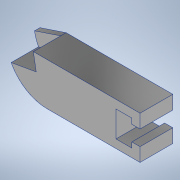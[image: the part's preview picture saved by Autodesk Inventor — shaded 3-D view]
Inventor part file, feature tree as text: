
AUTODESK INVENTOR PART (.ipt)
format: ipt  version: 2022 (Build 260153000, 153)  size: 172,032 bytes
history: native  units: mm
features: extrude x4, sketch x4, fillet x1
ambient origin geometry x8: Origin, YZ Plane, XZ Plane, XY Plane, X Axis, Y Axis, Z Axis, Center Point
bodies: Body1 (feature_tree)
feature tree (9):
  extrude  "Extrusion2"  Depth=5.8mm
  extrude  "Extrusion7"  Depth=12.0mm TaperAngle=0.0deg
  extrude  "Extrusion10"  Depth=15.6mm
  fillet  "Fillet2"  [1 undecoded]
  extrude  "Extrusion11"  Depth=5.6mm
  sketch  "Sketch5"  dims[d41=5.8mm d48=44.0mm]
  sketch  "Sketch11"  dims[d50=3.0mm d56=12.0mm d57=0.0mm]
  sketch  "Sketch14"  dims[d63=45.0mm d67=15.6mm d71=0.0mm]
  sketch  "Sketch15"  dims[d72=36.2mm d87=5.6mm d88=9.5mm d95=17.453293mm d96=6.0mm d97=15.0mm d98=10.0mm d99=0.0mm d107=10.0mm d108=0.0mm d109=0.0mm d110=15.0mm d111=10.0mm d112=0.0mm]
note: 1 required parameter value undecoded (feature->parameter linkage not recoverable at this tier; creation-order binding heuristic only, values carry confidence <= 0.55)
